# Revit family: HEM
name_source: partatom
category: Lighting Fixtures
units: mm (PartAtom-declared; Revit-internal decimal feet)

## family parameters
Cut with Voids When Loaded = No
Host = Face
Light Source = Yes
OmniClass Number = 23.80.70.11
OmniClass Title = Luminaries for Internal Lighting
Part Type = Normal
Room Calculation Point = No
Round Connector Dimension = Use Diameter
Shared = No

## types (6) — shared parameters
Backbox = Plastic -  White
Color Filter = 16777215
Connector Description = Lighting
Default Elevation = 48 "
Description = HEM is an enclosed and gasketed hazardous location LED product.
Dimming Lamp Color Temperature Shift = <None>
Emit Shape Visible in Rendering = Yes
Emit from Rectangle Length = 48 "
Emit from Rectangle Width = 5.78 "
Glass = Glass -  Frosted Lens
Lamp = LED Hazardous Location Enclosed and Gasketed
Manufacturer = Columbia Lighting
Model = HEM
Row Length = 48 "
Tilt Angle = -90.00°
URL = https://www.currentlighting.com
Voltage = 120 V

## per-type parameters (varying)
| type | Apparent Load | Lens | Lumen Output | Photometric Web File | Shielding | Wattage Comments |
| HEM4-40HL-DFA-EU | 54 VA | Lens : DFA Lens | High Lumen | HEM4-40HL-DFA-EU.IES | Deep Frosted Acrylic | 54W |
| HEM4-40HL-RFA-EU | 54 VA | Lens : RFA Lens | High Lumen | HEM4-40HL-RFA-EU.IES | Ribbed Frosted Acrylic | 54W |
| HEM4-40ML-DFA-EU | 54 VA | Lens : DFA Lens | Medium Lumen | HEM4-40HL-RFA-EU.IES | Deep Frosted Acrylic | 46W |
| HEM4-40ML-RFA-EU | 54 VA | Lens : RFA Lens | Medium Lumen | HEM4-40ML-RFA-EU.IES | Ribbed Frosted Acrylic | 46W |
| HEM4-40VL-DFA-EU | 68 VA | Lens : DFA Lens | Very High Lumen | HEM4-40VL-DFA-EU.IES | Deep Frosted Acrylic | 68W |
| HEM4-40VL-RFA-EU | 68 VA | Lens : RFA Lens | Very High Lumen | HEM4-40VL-RFA-EU.IES | Ribbed Frosted Acrylic | 68W |

## geometry (parser evidence)
native form markers: Blend x6, Sweep x5
no freeform markers — native parametric forms only
